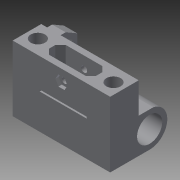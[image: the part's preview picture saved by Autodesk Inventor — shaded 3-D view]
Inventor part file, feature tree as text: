
AUTODESK INVENTOR PART (.ipt)
format: ipt  version: 2015 SP2 (Build 190223200, 223)  size: 219,648 bytes
history: native  units: mm
features: sketch x9, extrude x7, hole x3
ambient origin geometry x8: Origin, YZ Plane, XZ Plane, XY Plane, X Axis, Y Axis, Z Axis, Center Point
bodies: Solid1 (feature_tree)
feature tree (19):
  extrude  "Extrusion1"  Depth=39.0mm
  sketch  "Sketch2"  dims[d2=35.0mm d3=0.0mm d5=15.0mm]
  extrude  "Extrusion2"  Depth=15.0mm
  extrude  "Extrusion3"  Depth=8.0mm
  extrude  "Extrusion4"  Depth=17.0mm
  extrude  "Extrusion5"  Depth=10.0mm TaperAngle=0.0deg
  hole  "Hole1"  [1 undecoded]
  hole  "Hole2"  [1 undecoded]
  hole  "Hole3"  [1 undecoded]
  extrude  "Extrusion6"  Depth=28.0mm
  extrude  "Extrusion7"  Depth=3.5mm
  sketch  "Sketch1"  dims[d0=58.0mm d1=39.0mm]
  sketch  "Sketch3"  dims[d6=3.0mm d8=8.0mm]
  sketch  "Sketch4"  dims[d11=17.0mm d13=23.5mm]
  sketch  "Sketch5"  dims[d14=17.0mm d15=10.0mm d16=0.0mm]
  sketch  "Sketch7"  dims[d18=8.0mm d19=14.5mm d20=0.0mm]
  sketch  "Sketch8"  dims[d21=1.0mm d22=28.0mm]
  sketch  "Sketch9"  dims[d23=14.0mm d24=14.5mm d25=0.0mm]
  sketch  "Sketch10"  dims[d26=10.0mm d27=28.0mm d28=3.5mm d29=135.0deg d30=135.0deg d31=3.858mm d32=29.0mm d33=14.5mm d34=0.0mm d35=45.0mm d36=8.5mm d37=22.5mm d38=8.5mm d39=6.0mm d40=3.023mm d41=2.0mm d42=14.3117mm d43=37.0mm d44=0.0mm d45=14.0mm d46=7.0mm d47=3.6mm d48=6.0mm d49=6.2mm d50=2.0mm d51=14.3117mm d52=37.0mm d53=0.0mm d54=5.7mm d55=6.0mm d56=6.2mm d57=2.0mm d58=14.3117mm d59=23.5mm d60=0.0mm d63=3.6mm d64=2.0mm d65=0.0mm d66=4.5mm d67=5.0mm d68=0.0mm d71=6.5mm d72=17.0mm]
note: 3 required parameter values undecoded (feature->parameter linkage not recoverable at this tier; creation-order binding heuristic only, values carry confidence <= 0.55)
